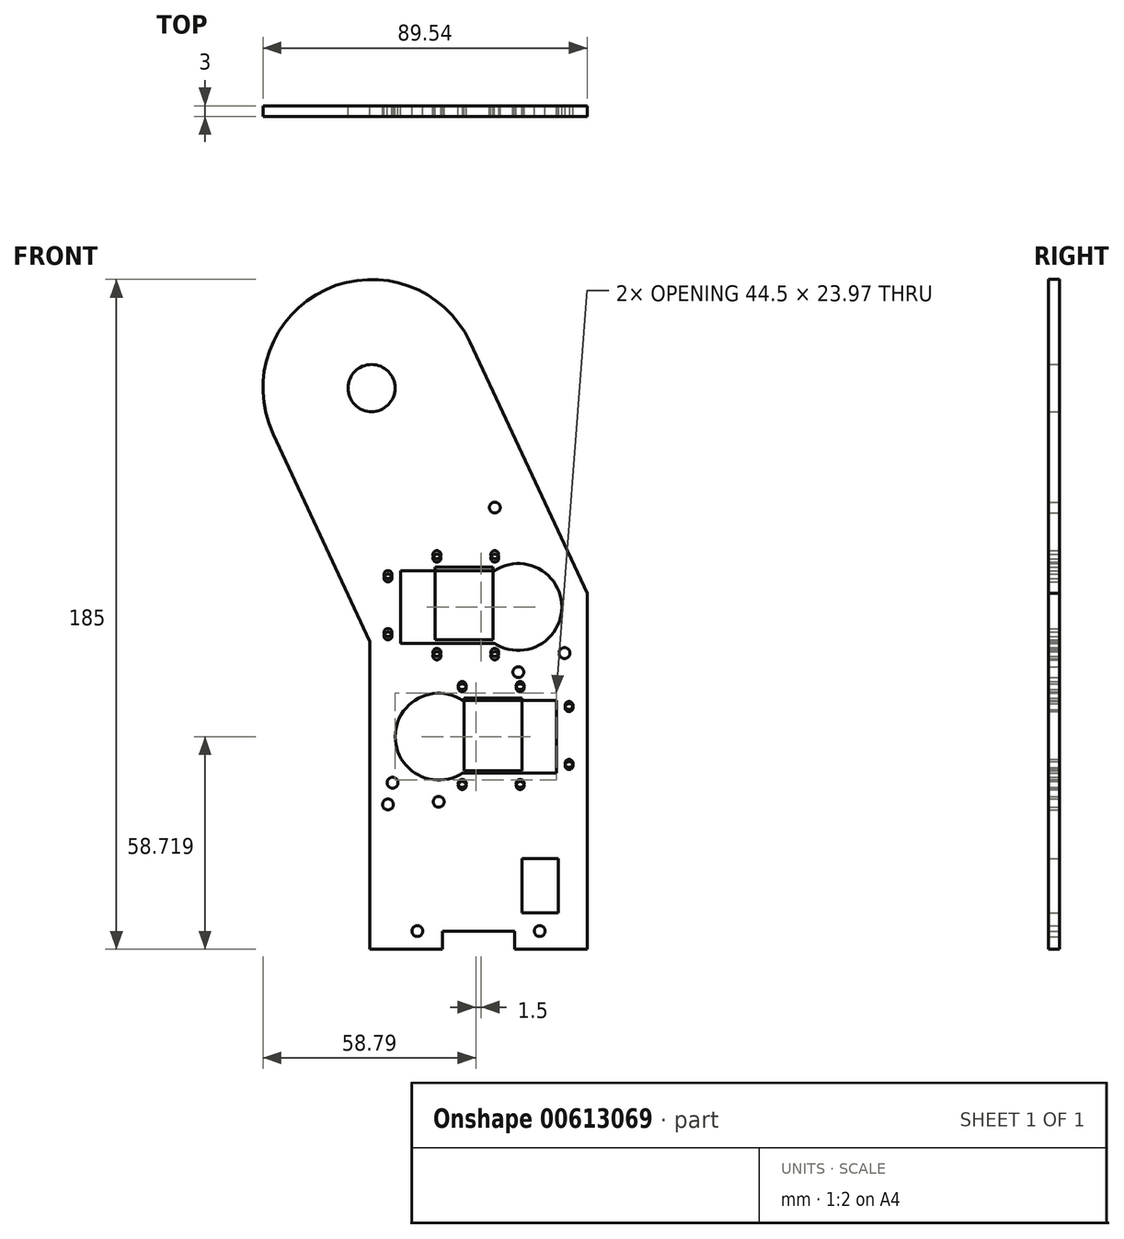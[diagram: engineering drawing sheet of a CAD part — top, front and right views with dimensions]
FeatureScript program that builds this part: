
annotation { "Feature Type Name" : "Feature", "Feature Type Description" : "" }
export const myFeature = defineFeature(function(context is Context, id is Id, definition is map)
    precondition{}
    {
        {
            var Q0;
            Q0=qCreatedBy(makeId("Front.planeOp"),FACE);
            var sketch = newSketch(context, id + "F0", { "sketchPlane" : qUnion([Q0])});
            skArc(sketch, "E0", {"start": v(-27.19, -12.68) * mm, "mid": v(-12.68, 27.19) * mm, "end": v(27.19, 12.68) * mm});
            skCircle(sketch, "E1", {"center": v(0, 0) * mm, "radius": 6.5 * mm});
            skLineSegment(sketch, "E2", {"start": v(-0.46, -150) * mm, "end": v(59.54, -150) * mm, "construction": true});
            skLineSegment(sketch, "E3", {"start": v(-0.46, -150) * mm, "end": v(-0.46, -70) * mm});
            skLineSegment(sketch, "E4", {"start": v(-0.46, -70) * mm, "end": v(-27.19, -12.68) * mm});
            skLineSegment(sketch, "E5", {"start": v(27.19, 12.68) * mm, "end": v(59.54, -56.7) * mm});
            skLineSegment(sketch, "E6", {"start": v(59.54, -56.7) * mm, "end": v(59.54, -150) * mm});
            skLineSegment(sketch, "E7", {"start": v(-0.46, -150) * mm, "end": v(-0.46, -155) * mm});
            skLineSegment(sketch, "E8", {"start": v(-0.46, -155) * mm, "end": v(19.54, -155) * mm});
            skLineSegment(sketch, "E9", {"start": v(19.54, -155) * mm, "end": v(19.54, -150) * mm});
            skLineSegment(sketch, "E10", {"start": v(39.54, -150) * mm, "end": v(39.54, -155) * mm});
            skLineSegment(sketch, "E11", {"start": v(39.54, -155) * mm, "end": v(59.54, -155) * mm});
            skLineSegment(sketch, "E12", {"start": v(59.54, -155) * mm, "end": v(59.54, -150) * mm});
            skLineSegment(sketch, "E13", {"start": v(19.54, -150) * mm, "end": v(39.54, -150) * mm});
            skCircle(sketch, "E14", {"center": v(18.54, -96.28) * mm, "radius": 12 * mm});
            skPoint(sketch, "E15", {"position": v(25.04, -82.78) * mm});
            skPoint(sketch, "E16", {"position": v(41.04, -82.78) * mm});
            skPoint(sketch, "E17", {"position": v(25.04, -109.78) * mm});
            skPoint(sketch, "E18", {"position": v(41.04, -109.78) * mm});
            skPoint(sketch, "E19", {"position": v(54.54, -104.28) * mm});
            skPoint(sketch, "E20", {"position": v(54.54, -88.28) * mm});
            skLineSegment(sketch, "E21", {"start": v(18.54, -96.28) * mm, "end": v(51.04, -96.28) * mm, "construction": true});
            skLineSegment(sketch, "E22", {"start": v(25.17, -86.28) * mm, "end": v(51.04, -86.28) * mm});
            skLineSegment(sketch, "E23", {"start": v(51.04, -86.28) * mm, "end": v(51.04, -106.28) * mm});
            skLineSegment(sketch, "E24", {"start": v(51.04, -106.28) * mm, "end": v(25.17, -106.28) * mm});
            skCircle(sketch, "E25", {"center": v(25.04, -82.78) * mm, "radius": 1.1 * mm});
            skCircle(sketch, "E26", {"center": v(41.04, -82.78) * mm, "radius": 1.1 * mm});
            skCircle(sketch, "E27", {"center": v(54.54, -88.28) * mm, "radius": 1.1 * mm});
            skCircle(sketch, "E28", {"center": v(54.54, -104.28) * mm, "radius": 1.1 * mm});
            skCircle(sketch, "E29", {"center": v(41.04, -109.78) * mm, "radius": 1.1 * mm});
            skCircle(sketch, "E30", {"center": v(25.04, -109.78) * mm, "radius": 1.1 * mm});
            skLineSegment(sketch, "E31.bottom", {"start": v(17.54, -49.5) * mm, "end": v(33.54, -49.5) * mm});
            skLineSegment(sketch, "E31.top", {"start": v(17.54, -69.5) * mm, "end": v(33.54, -69.5) * mm});
            skLineSegment(sketch, "E31.left", {"start": v(17.54, -49.5) * mm, "end": v(17.54, -69.5) * mm});
            skLineSegment(sketch, "E31.right", {"start": v(33.54, -49.5) * mm, "end": v(33.54, -69.5) * mm});
            skLineSegment(sketch, "E32", {"start": v(33.54, -59.5) * mm, "end": v(17.54, -59.5) * mm, "construction": true});
            skPoint(sketch, "E33", {"position": v(18.04, -46) * mm});
            skPoint(sketch, "E34", {"position": v(34.04, -46) * mm});
            skPoint(sketch, "E35", {"position": v(34.04, -73) * mm});
            skPoint(sketch, "E36", {"position": v(18.04, -73) * mm});
            skPoint(sketch, "E37", {"position": v(4.54, -51.5) * mm});
            skPoint(sketch, "E38", {"position": v(4.54, -67.5) * mm});
            skCircle(sketch, "E39", {"center": v(4.54, -51.5) * mm, "radius": 1.1 * mm});
            skCircle(sketch, "E40", {"center": v(4.54, -67.5) * mm, "radius": 1.1 * mm});
            skCircle(sketch, "E41", {"center": v(18.04, -73) * mm, "radius": 1.1 * mm});
            skCircle(sketch, "E42", {"center": v(34.04, -73) * mm, "radius": 1.1 * mm});
            skCircle(sketch, "E43", {"center": v(34.04, -46) * mm, "radius": 1.1 * mm});
            skCircle(sketch, "E44", {"center": v(18.04, -46) * mm, "radius": 1.1 * mm});
            skCircle(sketch, "E45", {"center": v(12.64, -150) * mm, "radius": 1.5 * mm});
            skCircle(sketch, "E46", {"center": v(46.44, -150) * mm, "radius": 1.5 * mm});
            skLineSegment(sketch, "E47", {"start": v(29.54, -150) * mm, "end": v(29.54, -144.6) * mm, "construction": true});
            skCircle(sketch, "E48", {"center": v(34.04, -33) * mm, "radius": 1.5 * mm});
            skCircle(sketch, "E49", {"center": v(4.54, -115) * mm, "radius": 1.5 * mm});
            skLineSegment(sketch, "E50.bottom", {"start": v(41.54, -130) * mm, "end": v(51.54, -130) * mm});
            skLineSegment(sketch, "E50.top", {"start": v(41.54, -145) * mm, "end": v(51.54, -145) * mm});
            skLineSegment(sketch, "E50.left", {"start": v(41.54, -130) * mm, "end": v(41.54, -145) * mm});
            skLineSegment(sketch, "E50.right", {"start": v(51.54, -130) * mm, "end": v(51.54, -145) * mm});
            skPoint(sketch, "E51", {"position": v(18.54, -114.28) * mm});
            skPoint(sketch, "E52", {"position": v(5.81, -109) * mm});
            skLineSegment(sketch, "E53", {"start": v(18.54, -96.28) * mm, "end": v(18.54, -114.28) * mm, "construction": true});
            skLineSegment(sketch, "E54", {"start": v(18.54, -96.28) * mm, "end": v(5.81, -109) * mm, "construction": true});
            skCircle(sketch, "E55", {"center": v(18.54, -114.28) * mm, "radius": 1.5 * mm});
            skCircle(sketch, "E56", {"center": v(5.81, -109) * mm, "radius": 1.5 * mm});
            skSolve(sketch);
        }
        {
            var Q0;
            Q0=qCreatedBy(makeId("Front.planeOp"),FACE);
            var sketch = newSketch(context, id + "F1", { "sketchPlane" : qUnion([Q0])});
            skArc(sketch, "E57", {"start": v(-27.19, -12.68) * mm, "mid": v(-12.68, 27.19) * mm, "end": v(27.19, 12.68) * mm});
            skCircle(sketch, "E58", {"center": v(0, 0) * mm, "radius": 6.5 * mm});
            skLineSegment(sketch, "E59", {"start": v(-0.46, -150) * mm, "end": v(59.54, -150) * mm, "construction": true});
            skLineSegment(sketch, "E60", {"start": v(-0.46, -150) * mm, "end": v(-0.46, -70) * mm});
            skLineSegment(sketch, "E61", {"start": v(-0.46, -70) * mm, "end": v(-27.19, -12.68) * mm});
            skLineSegment(sketch, "E62", {"start": v(27.19, 12.68) * mm, "end": v(59.54, -56.7) * mm});
            skLineSegment(sketch, "E63", {"start": v(59.54, -56.7) * mm, "end": v(59.54, -150) * mm});
            skLineSegment(sketch, "E64", {"start": v(-0.46, -150) * mm, "end": v(-0.46, -155) * mm});
            skLineSegment(sketch, "E65", {"start": v(-0.46, -155) * mm, "end": v(19.54, -155) * mm});
            skLineSegment(sketch, "E66", {"start": v(19.54, -155) * mm, "end": v(19.54, -150) * mm});
            skLineSegment(sketch, "E67", {"start": v(39.54, -150) * mm, "end": v(39.54, -155) * mm});
            skLineSegment(sketch, "E68", {"start": v(39.54, -155) * mm, "end": v(59.54, -155) * mm});
            skLineSegment(sketch, "E69", {"start": v(59.54, -155) * mm, "end": v(59.54, -150) * mm});
            skLineSegment(sketch, "E70", {"start": v(19.54, -150) * mm, "end": v(39.54, -150) * mm});
            skLineSegment(sketch, "E71.bottom", {"start": v(25.54, -85.67) * mm, "end": v(41.54, -85.67) * mm});
            skLineSegment(sketch, "E71.top", {"start": v(25.54, -105.67) * mm, "end": v(41.54, -105.67) * mm});
            skLineSegment(sketch, "E71.left", {"start": v(25.54, -85.67) * mm, "end": v(25.54, -105.67) * mm});
            skLineSegment(sketch, "E71.right", {"start": v(41.54, -85.67) * mm, "end": v(41.54, -105.67) * mm});
            skCircle(sketch, "E72", {"center": v(40.54, -60.47) * mm, "radius": 12 * mm});
            skLineSegment(sketch, "E73", {"start": v(40.54, -60.47) * mm, "end": v(8.04, -60.47) * mm, "construction": true});
            skLineSegment(sketch, "E74", {"start": v(8.04, -70.47) * mm, "end": v(8.04, -50.47) * mm});
            skLineSegment(sketch, "E75", {"start": v(8.04, -50.47) * mm, "end": v(33.9, -50.47) * mm});
            skLineSegment(sketch, "E76", {"start": v(8.04, -70.47) * mm, "end": v(33.9, -70.47) * mm});
            skPoint(sketch, "E77", {"position": v(18.04, -46.97) * mm});
            skPoint(sketch, "E78", {"position": v(34.04, -46.97) * mm});
            skPoint(sketch, "E79", {"position": v(18.04, -73.97) * mm});
            skPoint(sketch, "E80", {"position": v(34.04, -73.97) * mm});
            skPoint(sketch, "E81", {"position": v(4.54, -52.47) * mm});
            skPoint(sketch, "E82", {"position": v(4.54, -68.47) * mm});
            skCircle(sketch, "E83", {"center": v(18.04, -46.97) * mm, "radius": 1.1 * mm});
            skCircle(sketch, "E84", {"center": v(34.04, -46.97) * mm, "radius": 1.1 * mm});
            skCircle(sketch, "E85", {"center": v(34.04, -73.97) * mm, "radius": 1.1 * mm});
            skCircle(sketch, "E86", {"center": v(18.04, -73.97) * mm, "radius": 1.1 * mm});
            skCircle(sketch, "E87", {"center": v(4.54, -68.47) * mm, "radius": 1.1 * mm});
            skCircle(sketch, "E88", {"center": v(4.54, -52.47) * mm, "radius": 1.1 * mm});
            skLineSegment(sketch, "E89", {"start": v(25.54, -95.67) * mm, "end": v(41.54, -95.67) * mm, "construction": true});
            skPoint(sketch, "E90", {"position": v(54.54, -87.67) * mm});
            skPoint(sketch, "E91", {"position": v(54.54, -103.67) * mm});
            skPoint(sketch, "E92", {"position": v(25.04, -109.17) * mm});
            skPoint(sketch, "E93", {"position": v(41.04, -109.17) * mm});
            skPoint(sketch, "E94", {"position": v(41.04, -82.17) * mm});
            skPoint(sketch, "E95", {"position": v(25.04, -82.17) * mm});
            skCircle(sketch, "E96", {"center": v(25.04, -82.17) * mm, "radius": 1.1 * mm});
            skCircle(sketch, "E97", {"center": v(41.04, -82.17) * mm, "radius": 1.1 * mm});
            skCircle(sketch, "E98", {"center": v(54.54, -87.67) * mm, "radius": 1.1 * mm});
            skCircle(sketch, "E99", {"center": v(54.54, -103.67) * mm, "radius": 1.1 * mm});
            skCircle(sketch, "E100", {"center": v(41.04, -109.17) * mm, "radius": 1.1 * mm});
            skCircle(sketch, "E101", {"center": v(25.04, -109.17) * mm, "radius": 1.1 * mm});
            skLineSegment(sketch, "E102", {"start": v(29.54, -150) * mm, "end": v(29.54, -142.65) * mm, "construction": true});
            skCircle(sketch, "E103", {"center": v(46.44, -150) * mm, "radius": 1.5 * mm});
            skCircle(sketch, "E104", {"center": v(12.64, -150) * mm, "radius": 1.5 * mm});
            skCircle(sketch, "E105", {"center": v(34.04, -33) * mm, "radius": 1.5 * mm});
            skCircle(sketch, "E106", {"center": v(4.54, -115) * mm, "radius": 1.5 * mm});
            skLineSegment(sketch, "E107.bottom", {"start": v(41.54, -130) * mm, "end": v(51.54, -130) * mm});
            skLineSegment(sketch, "E107.top", {"start": v(41.54, -145) * mm, "end": v(51.54, -145) * mm});
            skLineSegment(sketch, "E107.left", {"start": v(41.54, -130) * mm, "end": v(41.54, -145) * mm});
            skLineSegment(sketch, "E107.right", {"start": v(51.54, -130) * mm, "end": v(51.54, -145) * mm});
            skLineSegment(sketch, "E108", {"start": v(40.54, -60.47) * mm, "end": v(40.54, -78.47) * mm, "construction": true});
            skLineSegment(sketch, "E109", {"start": v(40.54, -60.47) * mm, "end": v(53.27, -73.2) * mm, "construction": true});
            skCircle(sketch, "E110", {"center": v(53.27, -73.2) * mm, "radius": 1.5 * mm});
            skCircle(sketch, "E111", {"center": v(40.54, -78.47) * mm, "radius": 1.5 * mm});
            skSolve(sketch);
        }
        {
            var Q0;
            Q0=qSketchRegion(id+"F0",true);
            extrude(context, id + "F2", {"entities" : qUnion([Q0]), "depth" : 3 * mm, "offsetDistance" : 25 * mm});
        }
        {
            var Q0;
            Q0=qSketchRegion(id+"F1",true);
            extrude(context, id + "F3", {"entities" : qUnion([Q0]), "depth" : 3 * mm, "offsetDistance" : 25 * mm});
        }
    });
